FCSTD DOCUMENT  (FreeCAD 1.0R39109 (Git))
Label: tc2-main-pcb
License: All rights reserved
LicenseURL: http://en.wikipedia.org/wiki/All_rights_reserved
objects: Sketcher::SketchObject×2
note: 4 computed .brp shape members not serialized (recipe doc carries the construction recipe); baked Part::Feature solids carry a one-line shape summary decoded from their .brp

FEATURE [Sketcher::SketchObject] Sketch  label="features"
  ArcFitTolerance = 1e-06
  FullyConstrained = true
  MakeInternals = false
  MapMode = 5
  sketch-geometry (20):
    g0: LineSegment StartX=-2.5 StartY=25.25 StartZ=0 EndX=-2.5 EndY=-25.25 EndZ=0
    g1: LineSegment StartX=-2.5 StartY=-25.25 StartZ=0 EndX=2.5 EndY=-25.25 EndZ=0
    g2: LineSegment StartX=2.5 StartY=-25.25 StartZ=0 EndX=2.5 EndY=25.25 EndZ=0
    g3: LineSegment StartX=2.5 StartY=25.25 StartZ=0 EndX=-2.5 EndY=25.25 EndZ=0
    g4: Circle CenterX=0 CenterY=0 CenterZ=0 NormalX=0 NormalY=0 NormalZ=1 AngleXU=0 Radius=0.5
    g5: Circle CenterX=0 CenterY=29 CenterZ=0 NormalX=0 NormalY=0 NormalZ=1 AngleXU=0 Radius=1.5
    g6: Circle CenterX=-1e-16 CenterY=-29 CenterZ=0 NormalX=0 NormalY=0 NormalZ=1 AngleXU=0 Radius=1.5
    g7: Circle CenterX=8.2 CenterY=-24 CenterZ=0 NormalX=0 NormalY=0 NormalZ=1 AngleXU=0 Radius=1.5
    g8: Circle CenterX=8.2 CenterY=24 CenterZ=0 NormalX=0 NormalY=0 NormalZ=1 AngleXU=0 Radius=1.5
    g9: Circle CenterX=8.2 CenterY=33 CenterZ=0 NormalX=0 NormalY=0 NormalZ=1 AngleXU=0 Radius=0.5
    g10: Circle CenterX=-14.8 CenterY=33 CenterZ=0 NormalX=0 NormalY=0 NormalZ=1 AngleXU=0 Radius=0.5
    g11: Circle CenterX=-23 CenterY=29 CenterZ=0 NormalX=0 NormalY=0 NormalZ=1 AngleXU=0 Radius=1.5
    g12: Circle CenterX=-41.8 CenterY=29 CenterZ=0 NormalX=0 NormalY=0 NormalZ=1 AngleXU=0 Radius=1.5
    g13: Circle CenterX=-49 CenterY=29 CenterZ=0 NormalX=0 NormalY=0 NormalZ=1 AngleXU=0 Radius=1.5
    g14: Circle CenterX=-27.1 CenterY=-35.35 CenterZ=0 NormalX=0 NormalY=0 NormalZ=1 AngleXU=0 Radius=0.5
    g15: Circle CenterX=-30.6 CenterY=6.08 CenterZ=0 NormalX=0 NormalY=0 NormalZ=1 AngleXU=0 Radius=0.5
    g16: Circle CenterX=-30.6 CenterY=-24.92 CenterZ=0 NormalX=0 NormalY=0 NormalZ=1 AngleXU=0 Radius=0.5
    g17: Circle CenterX=-20.6 CenterY=-24.92 CenterZ=0 NormalX=0 NormalY=0 NormalZ=1 AngleXU=0 Radius=0.5
    g18: Circle CenterX=-49 CenterY=-21 CenterZ=0 NormalX=0 NormalY=0 NormalZ=1 AngleXU=0 Radius=1.5
    g19: Circle CenterX=-56.8 CenterY=-18 CenterZ=0 NormalX=0 NormalY=0 NormalZ=1 AngleXU=0 Radius=1.5
  constraints (55):
    c: Coincident(g0,g1)
    c: Coincident(g1,g2)
    c: Coincident(g2,g3)
    c: Coincident(g3,g0)
    c: Vertical(g0)
    c: Horizontal(g3)
    c: Symmetric(g2,g1,g-1)
    c: Symmetric(g0,g1,g-2)
    c: DistanceY(g2,g2) = 50.5
    c: DistanceX(g3,g3) = 5
    c: Coincident(g4,g-1)
    c: Diameter(g4) = 1
    c: PointOnObject(g5,g-2)
    c: Diameter(g5) = 3
    c: DistanceY(g4,g5) = 29
    c: Diameter(g6) = 3
    c: Symmetric(g6,g5,g-1)
    c: Diameter(g7) = 3
    c: DistanceX(g4,g7) = 8.2
    c: DistanceY(g7,g4) = 24
    c: Symmetric(g8,g7,g-1)
    c: Diameter(g8) = 3
    c: Diameter(g9) = 1
    c: Vertical(g8,g9)
    c: DistanceY(g4,g9) = 33
    c: Diameter(g10) = 1
    c: Horizontal(g9,g10)
    c: DistanceX(g10,g9) = 23
    c: Diameter(g11) = 3
    c: Horizontal(g11,g5)
    c: DistanceX(g11,g5) = 23
    c: Diameter(g12) = 3
    c: DistanceX(g12,g5) = 41.8
    c: Horizontal(g5,g12)
    c: Horizontal(g12,g13)
    c: DistanceX(g13,g5) = 49
    c: Diameter(g13) = 3
    c: Diameter(g14) = 1
    c: DistanceX(g14,g-1) = 27.1
    c: DistanceY(g14,g-1) = 35.35
    c: Diameter(g15) = 1
    c: DistanceY(g-1,g15) = 6.08
    c: DistanceX(g15,g-1) = 30.6
    c: Diameter(g16) = 1
    c: DistanceY(g16,g-1) = 24.92
    c: Vertical(g15,g16)
    c: Diameter(g17) = 1
    c: Horizontal(g17,g16)
    c: DistanceX(g16,g17) = 10
    c: Diameter(g18) = 3
    c: DistanceY(g18,g-1) = 21
    c: Vertical(g13,g18)
    c: Diameter(g19) = 3
    c: DistanceY(g19,g-1) = 18
    c: DistanceX(g19,g-1) = 56.8
FEATURE [Sketcher::SketchObject] Sketch001  label="boarder"
  ArcFitTolerance = 1e-06
  AttachmentSupport = -> [Sketch]
  ExternalGeometry = -> [Sketch]
  FullyConstrained = true
  MakeInternals = false
  MapMode = 2
  sketch-geometry (50):
    g0: LineSegment StartX=4.8 StartY=1.2 StartZ=0 EndX=4.8 EndY=19.2 EndZ=0
    g1: LineSegment StartX=5.8 StartY=20.2 StartZ=0 EndX=10.8 EndY=20.2 EndZ=0
    g2: LineSegment StartX=11.8 StartY=21.2 StartZ=0 EndX=11.8 EndY=35 EndZ=0
    g3: LineSegment StartX=-53.2 StartY=31.7 StartZ=0 EndX=-53.2 EndY=-13 EndZ=0
    g4: LineSegment StartX=-54.2 StartY=-14 StartZ=0 EndX=-60.2 EndY=-14 EndZ=0
    g5: LineSegment StartX=-61.2 StartY=-15 StartZ=0 EndX=-61.2 EndY=-24 EndZ=0
    g6: LineSegment StartX=-34.6 StartY=-33.5 StartZ=0 EndX=-34.6 EndY=-38.5 EndZ=0
    g7: LineSegment StartX=-33.6 StartY=-39.5 StartZ=0 EndX=-20.6 EndY=-39.5 EndZ=0
    g8: LineSegment StartX=-19.6 StartY=-38.5 StartZ=0 EndX=-19.6 EndY=-33.5 EndZ=0
    g9: LineSegment StartX=-18.6 StartY=-32.5 StartZ=0 EndX=10.8 EndY=-32.5 EndZ=0
    g10: LineSegment StartX=11.8 StartY=-31.5 StartZ=0 EndX=11.8 EndY=-0.8 EndZ=0
    g11: LineSegment StartX=10.8 StartY=0.2 StartZ=0 EndX=5.8 EndY=0.2 EndZ=0
    g12: ArcOfCircle CenterX=5.8 CenterY=1.2 CenterZ=0 NormalX=0 NormalY=0 NormalZ=1 AngleXU=0 Radius=1 StartAngle=3.14159 EndAngle=4.71239
    g13: GeomPoint [constr] X=4.8 Y=0.2 Z=0
    g14: ArcOfCircle CenterX=5.8 CenterY=19.2 CenterZ=0 NormalX=0 NormalY=0 NormalZ=1 AngleXU=0 Radius=1 StartAngle=1.5708 EndAngle=3.14159
    g15: GeomPoint [constr] X=4.8 Y=20.2 Z=0
    g16: ArcOfCircle CenterX=10.8 CenterY=21.2 CenterZ=0 NormalX=0 NormalY=0 NormalZ=1 AngleXU=0 Radius=1 StartAngle=4.71239 EndAngle=6.28319
    g17: GeomPoint [constr] X=11.8 Y=20.2 Z=0
    g18: ArcOfCircle CenterX=10.8 CenterY=-0.8 CenterZ=0 NormalX=0 NormalY=0 NormalZ=1 AngleXU=0 Radius=1 StartAngle=0 EndAngle=1.5708
    g19: GeomPoint [constr] X=11.8 Y=0.2 Z=0
    g20: ArcOfCircle CenterX=10.8 CenterY=-31.5 CenterZ=0 NormalX=0 NormalY=0 NormalZ=1 AngleXU=0 Radius=1 StartAngle=4.71239 EndAngle=6.28319
    g21: GeomPoint [constr] X=11.8 Y=-32.5 Z=0
    g22: ArcOfCircle CenterX=-18.6 CenterY=-33.5 CenterZ=0 NormalX=0 NormalY=0 NormalZ=1 AngleXU=0 Radius=1 StartAngle=1.5708 EndAngle=3.14159
    g23: GeomPoint [constr] X=-19.6 Y=-32.5 Z=0
    g24: ArcOfCircle CenterX=-20.6 CenterY=-38.5 CenterZ=0 NormalX=0 NormalY=0 NormalZ=1 AngleXU=0 Radius=1 StartAngle=4.71239 EndAngle=6.28319
    g25: GeomPoint [constr] X=-19.6 Y=-39.5 Z=0
    g26: ArcOfCircle CenterX=-33.6 CenterY=-38.5 CenterZ=0 NormalX=0 NormalY=0 NormalZ=1 AngleXU=0 Radius=1 StartAngle=3.14159 EndAngle=4.71239
    g27: GeomPoint [constr] X=-34.6 Y=-39.5 Z=0
    g28: ArcOfCircle CenterX=-35.6 CenterY=-33.5 CenterZ=0 NormalX=0 NormalY=0 NormalZ=1 AngleXU=0 Radius=1 StartAngle=0 EndAngle=1.5708
    g29: ArcOfCircle CenterX=-60.2 CenterY=-24 CenterZ=0 NormalX=0 NormalY=0 NormalZ=1 AngleXU=0 Radius=1 StartAngle=3.14159 EndAngle=4.71239
    g30: ArcOfCircle CenterX=-60.2 CenterY=-15 CenterZ=0 NormalX=0 NormalY=0 NormalZ=1 AngleXU=0 Radius=1 StartAngle=1.5708 EndAngle=3.14159
    g31: GeomPoint [constr] X=-61.2 Y=-14 Z=0
    g32: ArcOfCircle CenterX=-54.2 CenterY=-13 CenterZ=0 NormalX=0 NormalY=0 NormalZ=1 AngleXU=0 Radius=1 StartAngle=4.71239 EndAngle=6.28319
    g33: GeomPoint [constr] X=-53.2 Y=-14 Z=0
    g34: ArcOfCircle CenterX=-52.2 CenterY=31.7 CenterZ=0 NormalX=0 NormalY=0 NormalZ=1 AngleXU=0 Radius=1 StartAngle=1.5708 EndAngle=3.14159
    g35: ArcOfCircle CenterX=10.8 CenterY=35 CenterZ=0 NormalX=0 NormalY=0 NormalZ=1 AngleXU=0 Radius=1 StartAngle=-1.8e-15 EndAngle=1.5708
    g36: LineSegment StartX=-60.2 StartY=-25 StartZ=0 EndX=-54.2 EndY=-25 EndZ=0
    g37: LineSegment StartX=-53.2 StartY=-26 StartZ=0 EndX=-53.2 EndY=-31.5 EndZ=0
    g38: LineSegment StartX=-52.2 StartY=-32.5 StartZ=0 EndX=-35.6 EndY=-32.5 EndZ=0
    g39: ArcOfCircle CenterX=-54.2 CenterY=-26 CenterZ=0 NormalX=0 NormalY=0 NormalZ=1 AngleXU=0 Radius=1 StartAngle=9e-16 EndAngle=1.5708
    g40: GeomPoint [constr] X=-53.2 Y=-25 Z=0
    g41: ArcOfCircle CenterX=-52.2 CenterY=-31.5 CenterZ=0 NormalX=0 NormalY=0 NormalZ=1 AngleXU=0 Radius=1 StartAngle=3.14159 EndAngle=4.71239
    g42: GeomPoint [constr] X=-53.2 Y=-32.5 Z=0
    g43: LineSegment StartX=-52.2 StartY=32.7 StartZ=0 EndX=-34.7 EndY=32.7 EndZ=0
    g44: LineSegment StartX=-33.7 StartY=33.7 StartZ=0 EndX=-33.7 EndY=35 EndZ=0
    g45: LineSegment StartX=-32.7 StartY=36 StartZ=0 EndX=10.8 EndY=36 EndZ=0
    g46: ArcOfCircle CenterX=-34.7 CenterY=33.7 CenterZ=0 NormalX=0 NormalY=0 NormalZ=1 AngleXU=0 Radius=1 StartAngle=4.71239 EndAngle=6.28319
    g47: GeomPoint [constr] X=-33.7 Y=32.7 Z=0
    g48: ArcOfCircle CenterX=-32.7 CenterY=35 CenterZ=0 NormalX=0 NormalY=0 NormalZ=1 AngleXU=0 Radius=1 StartAngle=1.5708 EndAngle=3.14159
    g49: GeomPoint [constr] X=-33.7 Y=36 Z=0
  constraints (118):
    c: Vertical(g0)
    c: Horizontal(g1)
    c: Vertical(g2)
    c: Vertical(g3)
    c: Vertical(g5)
    c: Horizontal(g7)
    c: Vertical(g8)
    c: Horizontal(g9)
    c: Vertical(g10)
    c: Horizontal(g11)
    c: PointOnObject(g13,g0)
    c: PointOnObject(g13,g11)
    c: Tangent(g0,g12) = 1.5708
    c: Tangent(g11,g12) = 1.5708
    c: PointOnObject(g15,g0)
    c: PointOnObject(g15,g1)
    c: Tangent(g0,g14) = 1.5708
    c: Tangent(g1,g14) = 1.5708
    c: PointOnObject(g17,g1)
    c: PointOnObject(g17,g2)
    c: Tangent(g1,g16) = -1.5708
    c: Tangent(g2,g16) = -1.5708
    c: PointOnObject(g19,g10)
    c: PointOnObject(g19,g11)
    c: Tangent(g10,g18) = -1.5708
    c: Tangent(g11,g18) = -1.5708
    c: PointOnObject(g21,g9)
    c: PointOnObject(g21,g10)
    c: Tangent(g9,g20) = -1.5708
    c: Tangent(g10,g20) = -1.5708
    c: PointOnObject(g23,g8)
    c: PointOnObject(g23,g9)
    c: Tangent(g8,g22) = 1.5708
    c: Tangent(g9,g22) = 1.5708
    c: PointOnObject(g25,g7)
    c: PointOnObject(g25,g8)
    c: Tangent(g7,g24) = -1.5708
    c: Tangent(g8,g24) = -1.5708
    c: PointOnObject(g27,g6)
    c: PointOnObject(g27,g7)
    c: Tangent(g6,g26) = -1.5708
    c: Tangent(g7,g26) = -1.5708
    c: Tangent(g6,g28) = 1.5708
    c: Tangent(g5,g29) = -1.5708
    c: PointOnObject(g31,g4)
    c: PointOnObject(g31,g5)
    c: Tangent(g4,g30) = -1.5708
    c: Tangent(g5,g30) = -1.5708
    c: PointOnObject(g33,g3)
    c: PointOnObject(g33,g4)
    c: Tangent(g3,g32) = 1.5708
    c: Tangent(g4,g32) = 1.5708
    c: Tangent(g3,g34) = -1.5708
    c: Tangent(g2,g35) = -1.5708
    c: Equal(g14,g16)
    c: Equal(g14,g35)
    c: Equal(g14,g34)
    c: Equal(g14,g30)
    c: Equal(g14,g32)
    c: Equal(g14,g29)
    c: Equal(g14,g28)
    c: Equal(g14,g26)
    c: Equal(g14,g24)
    c: Equal(g14,g22)
    c: Equal(g14,g20)
    c: Equal(g14,g18)
    c: Equal(g14,g12)
    c: Radius(g14) = 1
    c: Horizontal(g4)
    c: Horizontal(g9,g28)
    c: Vertical(g6)
    c: Vertical(g2,g10)
    c: DistanceY(g11,g35) = 35.8
    c: DistanceY(g9,g35) = 68.5
    c: DistanceY(g1,g35) = 15.8
    c: DistanceY(g4,g35) = 50
    c: DistanceY(g7,g35) = 75.5
    c: Tangent(g29,g36) = -1.5708
    c: Vertical(g37)
    c: Horizontal(g38)
    c: PointOnObject(g40,g36)
    c: PointOnObject(g40,g37)
    c: Tangent(g36,g39) = 1.5708
    c: Tangent(g37,g39) = 1.5708
    c: PointOnObject(g42,g37)
    c: PointOnObject(g42,g38)
    c: Tangent(g37,g41) = -1.5708
    c: Tangent(g38,g41) = -1.5708
    c: Equal(g41,g39)
    c: Equal(g39,g29)
    c: Vertical(g3,g37)
    c: Horizontal(g36)
    c: Tangent(g38,g28) = 1.5708
    c: Tangent(g34,g43) = 1.5708
    c: Vertical(g44)
    c: Horizontal(g45)
    c: Horizontal(g43)
    c: PointOnObject(g47,g43)
    c: PointOnObject(g47,g44)
    c: Tangent(g43,g46) = -1.5708
    c: Tangent(g44,g46) = -1.5708
    c: PointOnObject(g49,g44)
    c: PointOnObject(g49,g45)
    c: Tangent(g44,g48) = 1.5708
    c: Tangent(g45,g48) = 1.5708
    c: Equal(g48,g46)
    c: Equal(g46,g34)
    c: DistanceX(g44,g2) = 45.5
    c: DistanceX(g3,g2) = 65
    c: DistanceY(g43,g35) = 3.3
    c: Tangent(g45,g35) = 1.5708
    c: DistanceX(g-1,g2) = 11.8
    c: DistanceX(g5,g2) = 73
    c: DistanceX(g8,g2) = 31.4
    c: DistanceX(g6,g2) = 46.4
    c: DistanceX(g0,g2) = 7
    c: DistanceY(g-1,g35) = 36
    c: DistanceY(g29,g4) = 11
